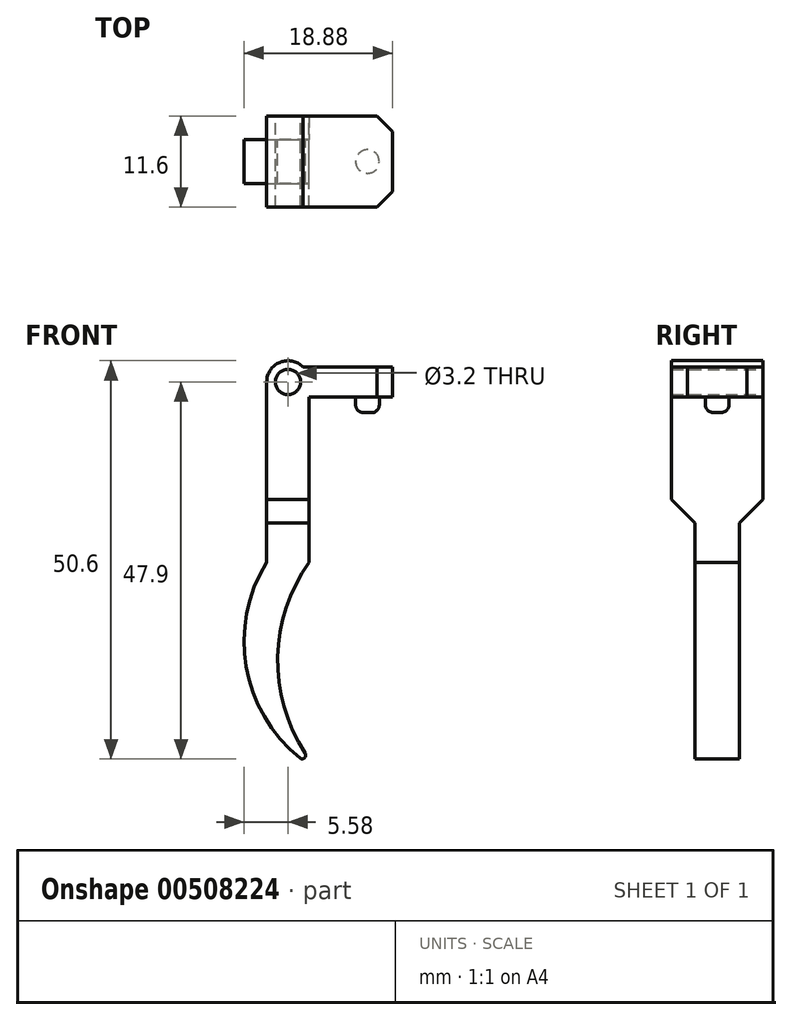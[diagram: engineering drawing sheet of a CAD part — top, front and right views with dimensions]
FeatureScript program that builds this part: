
annotation { "Feature Type Name" : "Feature", "Feature Type Description" : "" }
export const myFeature = defineFeature(function(context is Context, id is Id, definition is map)
    precondition{}
    {
        {
            var Q0;
            Q0=qCreatedBy(makeId("Front.planeOp"),FACE);
            var sketch = newSketch(context, id + "F0", { "sketchPlane" : qUnion([Q0])});
            skCircle(sketch, "E0", {"center": v(0, 0) * mm, "radius": 1.6 * mm});
            skCircle(sketch, "E1", {"center": v(0, 0) * mm, "radius": 2.7 * mm});
            skLineSegment(sketch, "E2", {"start": v(1.92, 1.9) * mm, "end": v(13.3, 1.9) * mm});
            skLineSegment(sketch, "E3", {"start": v(13.3, 1.9) * mm, "end": v(13.3, -1.9) * mm});
            skLineSegment(sketch, "E4", {"start": v(13.3, -1.9) * mm, "end": v(1.92, -1.9) * mm});
            skLineSegment(sketch, "E5", {"start": v(-2.7, 0) * mm, "end": v(-2.7, -22.9) * mm});
            skLineSegment(sketch, "E6", {"start": v(-2.7, -22.9) * mm, "end": v(2.7, -22.9) * mm});
            skLineSegment(sketch, "E7", {"start": v(2.7, -22.9) * mm, "end": v(2.7, -1.9) * mm});
            skArc(sketch, "E8", {"start": v(-2.7, -22.9) * mm, "mid": v(-5.29, -36.24) * mm, "end": v(1.7, -47.9) * mm});
            skArc(sketch, "E9", {"start": v(2.7, -22.9) * mm, "mid": v(-1.3, -35.4) * mm, "end": v(2.7, -47.9) * mm});
            skLineSegment(sketch, "E10", {"start": v(1.7, -47.9) * mm, "end": v(2.7, -47.9) * mm});
            skLineSegment(sketch, "E11", {"start": v(0, -22.9) * mm, "end": v(0, 0) * mm, "construction": true});
            skLineSegment(sketch, "E12", {"start": v(-2.7, -17.9) * mm, "end": v(2.7, -17.9) * mm});
            skSolve(sketch);
        }
        {
            var Q0;
            Q0=makeQuery(id+"F0.imprint","IMPRINT",FACE,{"disambiguationData":[TD([[makeQuery(id+"F0.imprint","IMPRINT",EDGE,{"derivedFrom":sQuery(id+"F0.wireOp",EDGE,"E0")}),-1.0]])]});
            var Q1;
            {var subQ3=sQuery(id+"F0.wireOp",EDGE,"E2");Q1=makeQuery(id+"F0.imprint","IMPRINT",FACE,{"disambiguationData":[TD([[makeQuery(id+"F0.imprint","IMPRINT",EDGE,{"derivedFrom":subQ3}),-1.0]])]});}
            var Q2;
            {var subQ3=sQuery(id+"F0.wireOp",EDGE,"E12");Q2=makeQuery(id+"F0.imprint","IMPRINT",FACE,{"disambiguationData":[TD([[makeQuery(id+"F0.imprint","IMPRINT",EDGE,{"derivedFrom":subQ3}),1.0]])]});}
            extrude(context, id + "F1", {"entities" : qUnion([Q0, Q1, Q2]), "depth" : 11.6 * mm, "offsetDistance" : 25 * mm, "symmetric" : true});
        }
        {
            var Q0;
            Q0=makeQuery(id+"F0.imprint","IMPRINT",FACE,{"disambiguationData":[TD([[makeQuery(id+"F0.imprint","IMPRINT",EDGE,{"derivedFrom":sQuery(id+"F0.wireOp",EDGE,"E6")}),-1.0]])]});
            var Q1;
            {var subQ0=sQuery(id+"F0.wireOp",EDGE,"E6");Q1=makeQuery(id+"F0.imprint","IMPRINT",FACE,{"disambiguationData":[TD([[makeQuery(id+"F0.imprint","IMPRINT",EDGE,{"derivedFrom":subQ0}),1.0]])]});}
            extrude(context, id + "F2", {"entities" : qUnion([Q0, Q1]), "operationType" : NewBodyOperationType.ADD, "depth" : 5.6 * mm, "offsetDistance" : 25 * mm, "symmetric" : true});
        }
        {
            var Q0;
            Q0=makeQuery(id+"F1.opExtrude","CAP_EDGE",EDGE,{"disambiguationData":[OSD([sQuery(id+"F0.wireOp",EDGE,"E12")])],"isStart":false});
            var Q1;
            Q1=makeQuery(id+"F1.opExtrude","CAP_EDGE",EDGE,{"disambiguationData":[OSD([sQuery(id+"F0.wireOp",EDGE,"E12")])],"isStart":true});
            chamfer(context, id + "F3", {"entities" : qUnion([Q0, Q1]), "width" : 3 * mm, "tangentPropagation" : true});
        }
        {
            var Q0;
            Q0=makeQuery(id+"F1.opExtrude","SWEPT_FACE",FACE,{"disambiguationData":[OSD([sQuery(id+"F0.wireOp",EDGE,"E4")])]});
            var sketch = newSketch(context, id + "F4", { "sketchPlane" : qUnion([Q0])});
            skCircle(sketch, "E13", {"center": v(10.1, 0) * mm, "radius": 1.5 * mm});
            skSolve(sketch);
        }
        {
            var Q0;
            Q0=makeQuery(id+"F4.imprint","IMPRINT",FACE,{"disambiguationData":[TD([[makeQuery(id+"F4.imprint","IMPRINT",EDGE,{"derivedFrom":sQuery(id+"F4.wireOp",EDGE,"E13")}),1.0]])]});
            extrude(context, id + "F5", {"entities" : qUnion([Q0]), "operationType" : NewBodyOperationType.ADD, "depth" : 2 * mm, "offsetDistance" : 25 * mm});
        }
        {
            var Q0;
            Q0=makeQuery(id+"F5.opExtrude","CAP_EDGE",EDGE,{"disambiguationData":[OSD([sQuery(id+"F4.wireOp",EDGE,"E13")])],"isStart":false});
            fillet(context, id + "F6", {"entities" : qUnion([Q0]), "radius" : 1 * mm, "tangentPropagation" : true, "allowEdgeOverflow" : false});
        }
        {
            var Q0;
            Q0=makeQuery(id+"F2.opExtrude","SWEPT_EDGE",EDGE,{"disambiguationData":[OSD([sQuery(id+"F0.wireOp",EDGE,"E8"),sQuery(id+"F0.wireOp",EDGE,"E10")])]});
            var Q1;
            Q1=makeQuery(id+"F2.opExtrude","SWEPT_EDGE",EDGE,{"disambiguationData":[OSD([sQuery(id+"F0.wireOp",EDGE,"E9"),sQuery(id+"F0.wireOp",EDGE,"E10")])]});
            fillet(context, id + "F7", {"entities" : qUnion([Q0, Q1]), "radius" : 0.5 * mm, "tangentPropagation" : true, "allowEdgeOverflow" : false});
        }
        {
            var Q0;
            Q0=makeQuery(id+"F1.opExtrude","CAP_EDGE",EDGE,{"disambiguationData":[OSD([sQuery(id+"F0.wireOp",EDGE,"E3")])],"isStart":false});
            var Q1;
            Q1=makeQuery(id+"F1.opExtrude","CAP_EDGE",EDGE,{"disambiguationData":[OSD([sQuery(id+"F0.wireOp",EDGE,"E3")])],"isStart":true});
            chamfer(context, id + "F8", {"entities" : qUnion([Q0, Q1]), "width" : 2 * mm, "tangentPropagation" : true});
        }
    });
